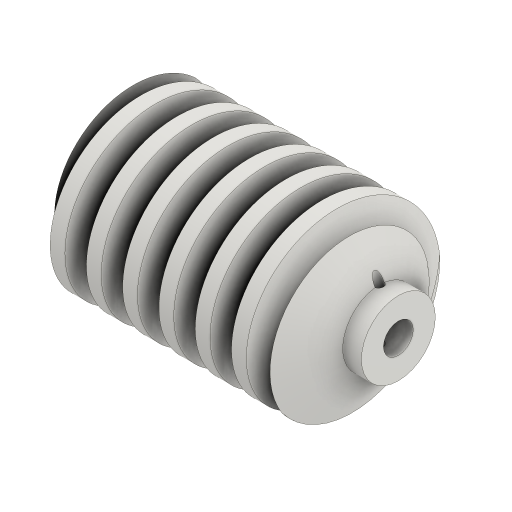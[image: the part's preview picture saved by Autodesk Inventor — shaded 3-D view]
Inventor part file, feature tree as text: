
AUTODESK INVENTOR PART (.ipt)
format: ipt  version: 2024.1 (Build 281209000, 209)  size: 505,344 bytes
history: native  units: mm (DEFAULTED — no unit token found)
features: other x8, extrude x3, sketch x3, chamfer x2, pattern_circular x2, revolve x1, reference x1
ambient origin geometry x6: Origin, XZ Plane, X Axis, Y Axis, Z Axis, Center Point
bodies: Solid1 (feature_tree)
feature tree (20):
  extrude  "Grundkörper"  Depth=19.0mm
  chamfer  "Chamfer1"  Distance=1.000918mm
  chamfer  "Chamfer2"  Distance=2.75mm
  other  "Zahnskizze"
  other  "Zahn"
  pattern_circular  "Zahnanordnung"  [2 undecoded]
  other  "Linker Zahn"
  pattern_circular  "Linke Zahnanordnung"  [2 undecoded]
  extrude  "Extrusion2"  Depth=4.0mm
  extrude  "Extrusion3"  Depth=4.0mm
  revolve  "Umdrehung1"
  other  "Grundkörperskizze"
  other  "Srf1"
  sketch  "Skizze6"  dims[d4=40.0mm d5=19.0mm]
  reference  "Referenz1"
  sketch  "Skizze7"  dims[d6=30.0mm]
  sketch  "Skizze8"  dims[d7=0.0mm d8=1.000918mm d9=2.75mm d10=1.000918mm d11=2.75mm d12=19.198622mm d14=3.1425mm d24=19.198622mm d25=21.20575mm d26=0.981748mm d27=7.0mm d28=9.0mm d29=10.7mm d30=22.5deg d31=10.0mm d32=100.0mm d33=0.0mm d34=90.0deg d35=90.0deg d36=0.0mm d37=0.0mm d44=10.0mm d46=360.0deg d47=45.0deg d48=45.0deg d49=28.975mm d50=0.0mm d54=0.0mm d56=0.0mm d59=18.75mm d60=10.0mm d61=0.0mm d62=22.5deg d63=10.0mm d64=150.0mm d65=0.0mm d66=90.0deg d67=90.0deg d68=0.0mm d69=0.0mm d70=10.0mm d71=10.0mm d72=10.0mm d73=360.0deg d75=10.0mm d76=10.0mm d77=0.0mm d79=28.975mm d80=0.0mm d81=0.0mm d82=0.089012mm d83=1.0mm d84=0.0mm d85=0.0mm d86=2.7mm d87=4.0mm d88=90.0deg]
  other  "Flankendurchmesser"
  other  "Assembly_Planktoscope_Uc2version_wormdrive_V3.iam"
  other  "00_NEMA11:1"
note: 4 required parameter values undecoded (feature->parameter linkage not recoverable at this tier; creation-order binding heuristic only, values carry confidence <= 0.55)
